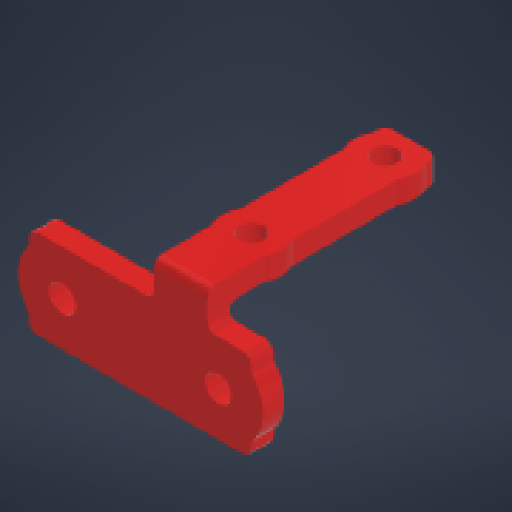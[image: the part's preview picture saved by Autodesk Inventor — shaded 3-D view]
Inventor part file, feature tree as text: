
AUTODESK INVENTOR PART (.ipt)
format: ipt  version: 2024.1 (Build 281209000, 209)  size: 237,056 bytes
history: native  units: in
note: dims shown in document units (in); Inventor stores cm internally (conversion verified against a paired STEP export)
features: extrude x2, sketch x2, projected_geometry x2, direct_edit x1, imported_body x1, other x1
ambient origin geometry x8: Origin, YZ Plane, XZ Plane, XY Plane, X Axis, Y Axis, Z Axis, Center Point
bodies: Solid1 (feature_tree)
feature tree (9):
  direct_edit  "Direct Edit1"
  extrude  "Extrusion1"  Depth=0.3937in TaperAngle=0.0deg
  extrude  "Extrusion2"  Depth=0.3937in
  sketch  "Sketch1"  dims[d0=8.7087in d1=0.3937in d2=0.3937in d3=0.3937in d4=0.0in]
  projected_geometry  "Projected Loop1"
  sketch  "Sketch2"  dims[d5=11.811in d6=11.811in d7=0.3937in d8=0.0in]
  projected_geometry  "Projected Loop2"
  imported_body  "Base1"
  other  "Scale1"
